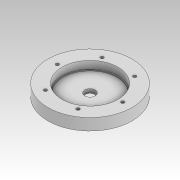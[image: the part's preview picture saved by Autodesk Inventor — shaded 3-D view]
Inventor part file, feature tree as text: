
AUTODESK INVENTOR PART (.ipt)
format: ipt  version: 2020 (Build 240168000, 168)  size: 237,568 bytes
history: native  units: mm
features: sketch x3, extrude x2, revolve x1, pattern_circular x1
ambient origin geometry x8: Origin, YZ Plane, XZ Plane, XY Plane, X Axis, Y Axis, Z Axis, Center Point
bodies: Body1 (feature_tree)
feature tree (7):
  revolve  "Revolution2"  [1 undecoded]
  extrude  "Extrusion18"  Depth=29.5mm
  extrude  "Extrusion19"  Depth=45.0mm
  pattern_circular  "Circular Pattern3"  [2 undecoded]
  sketch  "Sketch19"  dims[d90=0.5mm d91=5.6mm]
  sketch  "Sketch20"  dims[d92=1.0mm d93=29.5mm]
  sketch  "Sketch21"  dims[d94=40.5mm d95=45.0mm d96=1.0mm d97=1.0mm d99=30.0mm d100=1.0mm d101=8.0mm d102=90.0deg d103=3.0mm d104=70.0mm d105=3.5mm d106=0.0mm d107=0.0mm d108=5.8mm d109=5.8mm d110=3.0mm d111=0.0mm d112=60.0mm d113=360.0deg d64=0.5mm d65=0.872665mm d66=0.5mm d67=0.872665mm]
note: 3 required parameter values undecoded (feature->parameter linkage not recoverable at this tier; creation-order binding heuristic only, values carry confidence <= 0.55)